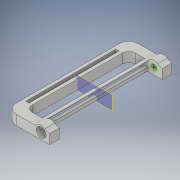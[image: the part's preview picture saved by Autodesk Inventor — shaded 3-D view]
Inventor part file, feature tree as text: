
AUTODESK INVENTOR PART (.ipt)
format: ipt  version: 2018 (Build 220112000, 112)  size: 228,352 bytes
history: native  units: in
note: dims shown in document units (in); Inventor stores cm internally (conversion verified against a paired STEP export)
features: sketch x15, extrude x9, fillet x6, hole x2, plane x1, mirror x1
ambient origin geometry x8: Origin, YZ Plane, XZ Plane, XY Plane, X Axis, Y Axis, Z Axis, Center Point
bodies: Solid1 (feature_tree)
feature tree (34):
  extrude  "Extrusion1"  Depth=0.375in
  sketch  "Sketch2"  dims[d3=0.375in d4=0.5in d5=0.375in d6=0.0in]
  extrude  "Extrusion2"  Depth=0.375in
  fillet  "Fillet1"  Radius=0.375in
  extrude  "Extrusion3"  Depth=0.375in
  extrude  "Extrusion4"  Depth=0.25in
  plane  "Work Plane1"
  mirror  "Mirror1"
  fillet  "Fillet2"  Radius=0.24in
  extrude  "Extrusion5"  Depth=0.375in
  sketch  "Sketch6"  dims[d17=1.0in d18=0.0in d19=0.24in d20=0.0in]
  extrude  "Extrusion6"  Depth=0.24in TaperAngle=0.0deg
  extrude  "Extrusion7"  Depth=0.375in
  fillet  "Fillet3"  Radius=0.25in
  fillet  "Fillet4"  Radius=0.375in
  fillet  "Fillet5"  Radius=0.25in
  fillet  "Fillet6"  Radius=0.125in
  sketch  "Sketch9"  dims[d30=0.125in d31=0.125in]
  extrude  "Extrusion8"  Depth=0.035in
  sketch  "Sketch11"  dims[d35=0.2in]
  sketch  "Sketch12"  dims[d36=0.2in d37=0.75in d38=0.375in d39=0.25in d40=0.5635in d41=0.35in d42=0.0in]
  hole  "Hole1"  [1 undecoded]
  hole  "Hole2"  [1 undecoded]
  sketch  "Sketch14"  dims[d51=3.5in]
  extrude  "Extrusion9"  Depth=0.125in
  sketch  "Sketch1"  dims[d0=1.3in d1=0.375in]
  sketch  "Sketch3"  dims[d7=0.375in d8=0.0in d9=0.375in]
  sketch  "Sketch4"  dims[d10=0.24in d11=0.0in d12=0.25in d13=0.24in d14=0.0in]
  sketch  "Sketch5"  dims[d15=2.0in d16=0.375in]
  sketch  "Sketch7"  dims[d21=0.375in d22=0.0in d23=0.375in d24=0.25in d25=0.375in d26=0.25in d27=0.125in]
  sketch  "Sketch8"  dims[d28=0.035in d29=0.035in]
  sketch  "Sketch10"  dims[d32=4.375in d33=0.0in d34=0.2in]
  sketch  "Sketch13"  dims[d43=0.2in d44=0.75in d45=0.375in d46=0.25in d47=0.5635in d48=0.35in d49=0.0in d50=0.125in]
  sketch  "Sketch15"  dims[d52=0.375in d53=0.0in]
note: 2 required parameter values undecoded (feature->parameter linkage not recoverable at this tier; creation-order binding heuristic only, values carry confidence <= 0.55)
